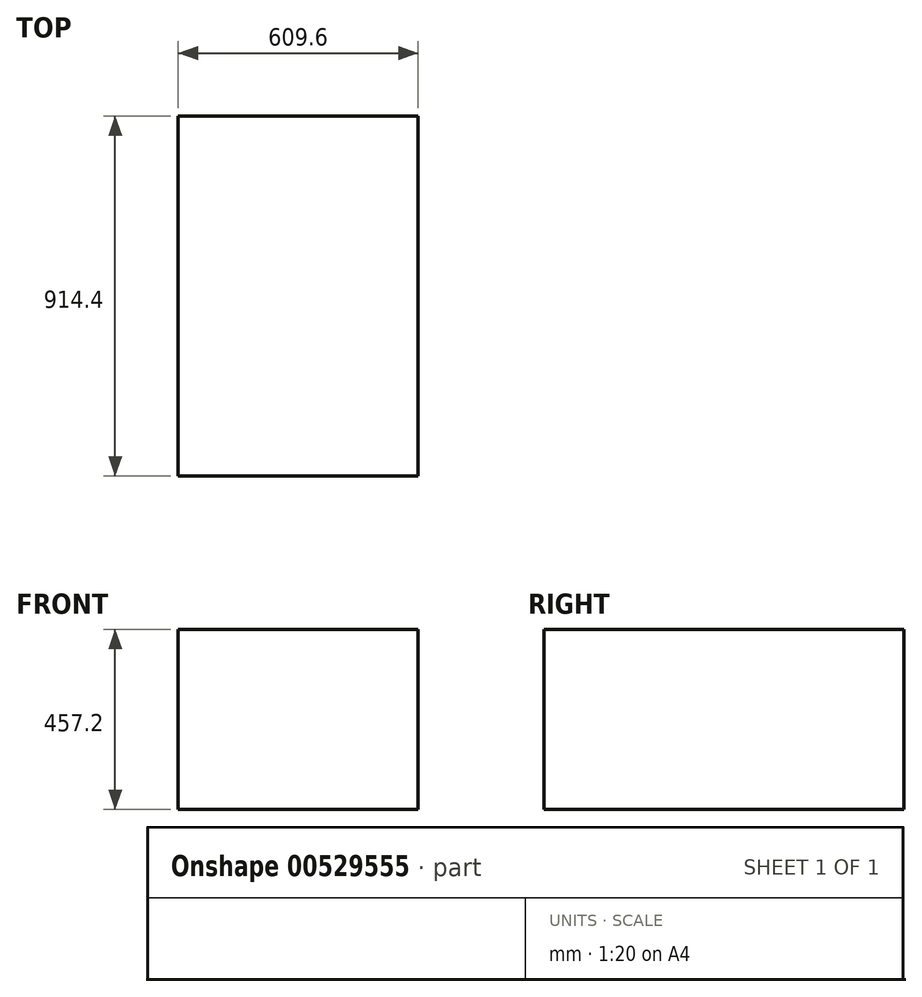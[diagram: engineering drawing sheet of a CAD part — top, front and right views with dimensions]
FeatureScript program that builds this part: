
annotation { "Feature Type Name" : "Feature", "Feature Type Description" : "" }
export const myFeature = defineFeature(function(context is Context, id is Id, definition is map)
    precondition{}
    {
        {
            var Q0;
            Q0=qCreatedBy(makeId("Top.planeOp"),FACE);
            var sketch = newSketch(context, id + "F0", { "sketchPlane" : qUnion([Q0])});
            skLineSegment(sketch, "E0.bottom", {"start": v(-609.6, 390.75) * mm, "end": v(0, 390.75) * mm});
            skLineSegment(sketch, "E0.top", {"start": v(-609.6, -523.65) * mm, "end": v(0, -523.65) * mm});
            skLineSegment(sketch, "E0.left", {"start": v(-609.6, 390.75) * mm, "end": v(-609.6, -523.65) * mm});
            skLineSegment(sketch, "E0.right", {"start": v(0, 390.75) * mm, "end": v(0, -523.65) * mm});
            skSolve(sketch);
        }
        {
            var Q0;
            Q0=makeQuery(id+"F0.imprint","IMPRINT",FACE,{"disambiguationData":[TD([[makeQuery(id+"F0.imprint","IMPRINT",EDGE,{"derivedFrom":sQuery(id+"F0.wireOp",EDGE,"E0.bottom")}),-1.0]])]});
            extrude(context, id + "F1", {"entities" : qUnion([Q0]), "depth" : 457.2 * mm, "offsetDistance" : 30.48 * mm});
        }
    });
